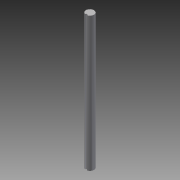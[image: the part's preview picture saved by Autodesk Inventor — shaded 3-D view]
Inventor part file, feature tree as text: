
AUTODESK INVENTOR PART (.ipt)
format: ipt  version: 2013 (Build 170138000, 138)  size: 72,192 bytes
history: native  units: in
note: dims shown in document units (in); Inventor stores cm internally (conversion verified against a paired STEP export)
features: extrude x1, sketch x1
ambient origin geometry x8: Origin, YZ Plane, XZ Plane, XY Plane, X Axis, Y Axis, Z Axis, Center Point
bodies: Solid1 (feature_tree)
feature tree (2):
  extrude  "Extrusion1"  Depth=0.0787in
  sketch  "Sketch1"  dims[d0=0.315in d1=0.0787in d2=0.0394in d3=0.0394in d4=5.25in d5=0.0in]
